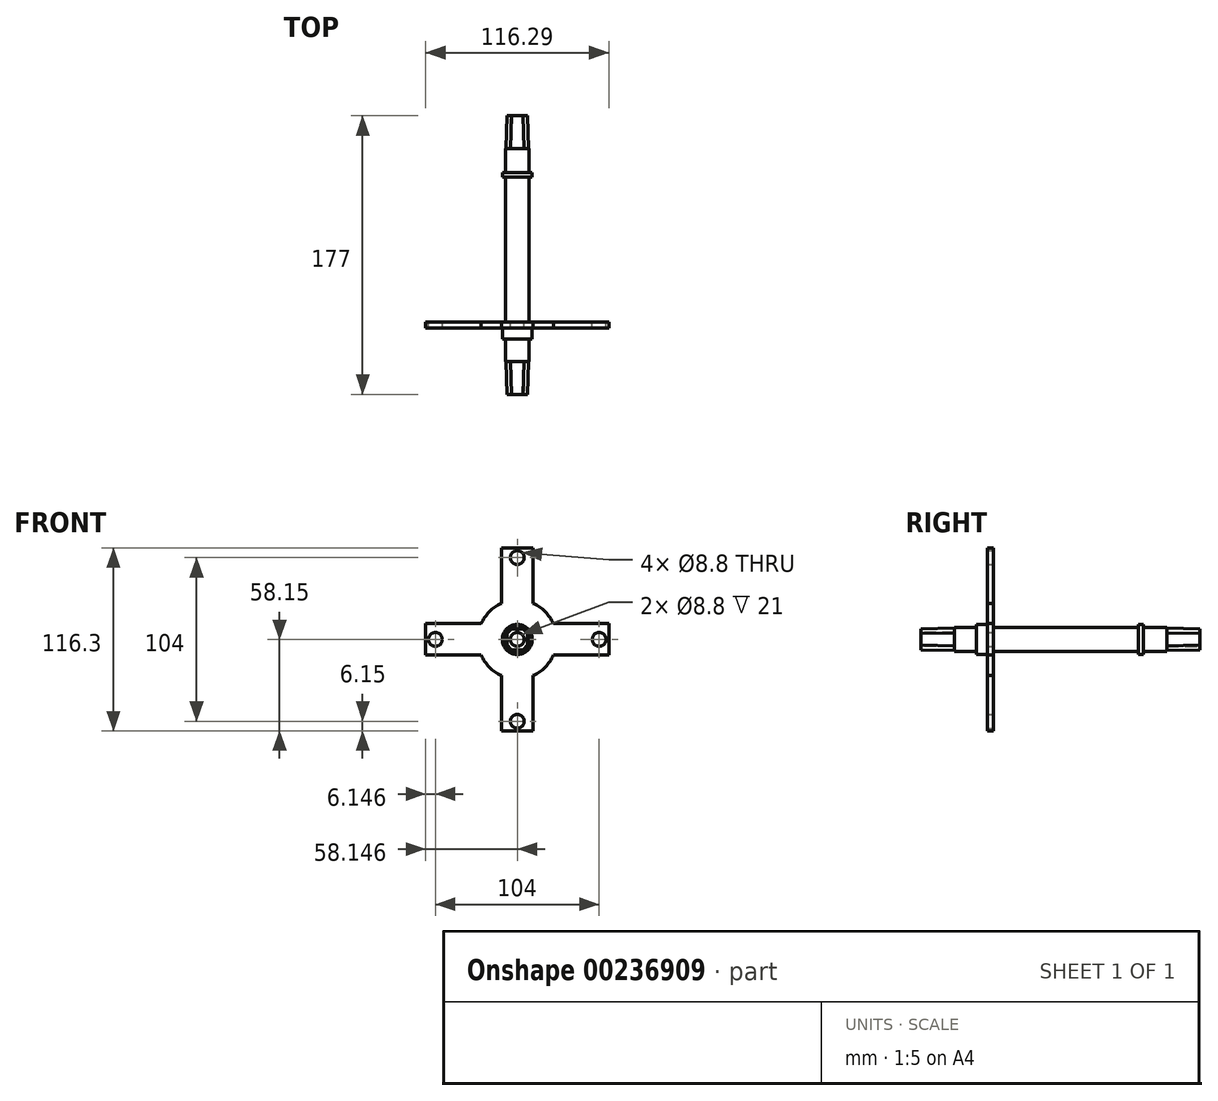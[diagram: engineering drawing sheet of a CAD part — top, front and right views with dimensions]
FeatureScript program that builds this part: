
annotation { "Feature Type Name" : "Feature", "Feature Type Description" : "" }
export const myFeature = defineFeature(function(context is Context, id is Id, definition is map)
    precondition{}
    {
        {
            var Q0;
            Q0=qCreatedBy(makeId("Front.planeOp"),FACE);
            cPlane(context, id + "F0", {"entities" : qUnion([Q0]), "cplaneType" : CPlaneType.OFFSET, "offset" : 135 * mm, "oppositeDirection" : true, "width" : 150 * mm, "height" : 150 * mm});
        }
        {
            var Q0;
            Q0=qCreatedBy(makeId("Front.planeOp"),FACE);
            cPlane(context, id + "F1", {"entities" : qUnion([Q0]), "cplaneType" : CPlaneType.OFFSET, "offset" : 67.5 * mm, "oppositeDirection" : true, "width" : 150 * mm, "height" : 150 * mm});
        }
        {
            var Q0;
            Q0=qCreatedBy(makeId("Front.planeOp"),FACE);
            cPlane(context, id + "F2", {"entities" : qUnion([Q0]), "cplaneType" : CPlaneType.OFFSET, "offset" : 21 * mm, "width" : 150 * mm, "height" : 150 * mm});
        }
        {
            var Q0;
            Q0=qCreatedBy(makeId("Front.planeOp"),FACE);
            var sketch = newSketch(context, id + "F3", { "sketchPlane" : qUnion([Q0])});
            skLineSegment(sketch, "E0.bottom", {"start": v(-101.97, -7.15) * mm, "end": v(-116.27, -7.15) * mm});
            skLineSegment(sketch, "E0.top", {"start": v(-101.97, 7.15) * mm, "end": v(-116.27, 7.15) * mm});
            skLineSegment(sketch, "E0.left", {"start": v(-101.97, -7.15) * mm, "end": v(-101.97, 7.15) * mm});
            skLineSegment(sketch, "E0.right", {"start": v(-116.27, -7.15) * mm, "end": v(-116.27, 7.15) * mm});
            skPoint(sketch, "E0.middle", {"position": v(-109.12, 0) * mm});
            skSolve(sketch);
        }
        {
            var Q0;
            Q0=qCreatedBy(id+"F2.planeOp",FACE);
            var sketch = newSketch(context, id + "F4", { "sketchPlane" : qUnion([Q0])});
            skLineSegment(sketch, "E1.bottom", {"start": v(-102.47, 6.65) * mm, "end": v(-115.77, 6.65) * mm});
            skLineSegment(sketch, "E1.top", {"start": v(-102.47, -6.65) * mm, "end": v(-115.77, -6.65) * mm});
            skLineSegment(sketch, "E1.left", {"start": v(-102.47, 6.65) * mm, "end": v(-102.47, -6.65) * mm});
            skLineSegment(sketch, "E1.right", {"start": v(-115.77, 6.65) * mm, "end": v(-115.77, -6.65) * mm});
            skPoint(sketch, "E1.middle", {"position": v(-109.12, 0) * mm});
            skSolve(sketch);
        }
        {
            var Q0;
            Q0=sQuery(id+"F4.wireOp",VERTEX,"E1.middle");
            var Q1;
            Q1=qCreatedBy(makeId("Right.planeOp"),FACE);
            cPlane(context, id + "F5", {"entities" : qUnion([Q0, Q1]), "cplaneType" : CPlaneType.PLANE_POINT, "offset" : 25 * mm, "width" : 150 * mm, "height" : 150 * mm});
        }
        {
            var Q0;
            Q0=qCreatedBy(id+"F5.planeOp",FACE);
            var sketch = newSketch(context, id + "F6", { "sketchPlane" : qUnion([Q0])});
            skLineSegment(sketch, "E2", {"start": v(-85.2, 0) * mm, "end": v(164.36, 0) * mm, "construction": true});
            skSolve(sketch);
        }
        {
            var Q0;
            Q0=makeQuery(id+"F3.imprint","IMPRINT",FACE,{"disambiguationData":[TD([[makeQuery(id+"F3.imprint","IMPRINT",EDGE,{"derivedFrom":sQuery(id+"F3.wireOp",EDGE,"E0.bottom")}),-1.0]])]});
            var Q1;
            Q1=makeQuery(id+"F4.imprint","IMPRINT",FACE,{"disambiguationData":[TD([[makeQuery(id+"F4.imprint","IMPRINT",EDGE,{"derivedFrom":sQuery(id+"F4.wireOp",EDGE,"E1.bottom")}),1.0]])]});
            loft(context, id + "F7", {"sheetProfilesArray" : [{ "sheetProfileEntities" : qUnion([Q0]) }, { "sheetProfileEntities" : qUnion([Q1]) }]});
        }
        {
            var Q0;
            Q0=makeQuery(id+"F7.opLoft","SWEPT_EDGE",EDGE,{"disambiguationData":[OSD([sQuery(id+"F3.wireOp",EDGE,"E0.top"),sQuery(id+"F3.wireOp",EDGE,"E0.right"),sQuery(id+"F4.wireOp",EDGE,"E1.bottom"),sQuery(id+"F4.wireOp",EDGE,"E1.right")])]});
            var Q1;
            Q1=makeQuery(id+"F7.opLoft","SWEPT_EDGE",EDGE,{"disambiguationData":[OSD([sQuery(id+"F3.wireOp",EDGE,"E0.bottom"),sQuery(id+"F3.wireOp",EDGE,"E0.right"),sQuery(id+"F4.wireOp",EDGE,"E1.top"),sQuery(id+"F4.wireOp",EDGE,"E1.right")])]});
            var Q2;
            Q2=makeQuery(id+"F7.opLoft","SWEPT_EDGE",EDGE,{"disambiguationData":[OSD([sQuery(id+"F3.wireOp",EDGE,"E0.top"),sQuery(id+"F3.wireOp",EDGE,"E0.left"),sQuery(id+"F4.wireOp",EDGE,"E1.bottom"),sQuery(id+"F4.wireOp",EDGE,"E1.left")])]});
            var Q3;
            Q3=makeQuery(id+"F7.opLoft","SWEPT_EDGE",EDGE,{"disambiguationData":[OSD([sQuery(id+"F3.wireOp",EDGE,"E0.bottom"),sQuery(id+"F3.wireOp",EDGE,"E0.left"),sQuery(id+"F4.wireOp",EDGE,"E1.top"),sQuery(id+"F4.wireOp",EDGE,"E1.left")])]});
            chamfer(context, id + "F8", {"entities" : qUnion([Q0, Q1, Q2, Q3]), "width" : 3 * mm, "tangentPropagation" : true});
        }
        {
            var Q0;
            Q0=qCreatedBy(makeId("Front.planeOp"),FACE);
            var sketch = newSketch(context, id + "F9", { "sketchPlane" : qUnion([Q0])});
            skCircle(sketch, "E3", {"center": v(-109.12, 0) * mm, "radius": 7.5 * mm});
            skCircle(sketch, "E4", {"center": v(-109.12, 0) * mm, "radius": 9.5 * mm});
            skSolve(sketch);
        }
        {
            var Q0;
            Q0=makeQuery(id+"F9.imprint","IMPRINT",FACE,{"disambiguationData":[TD([[makeQuery(id+"F9.imprint","IMPRINT",EDGE,{"derivedFrom":sQuery(id+"F9.wireOp",EDGE,"E3")}),1.0]])]});
            var Q1;
            Q1=qCreatedBy(id+"F0.planeOp",FACE);
            extrude(context, id + "F10", {"entities" : qUnion([Q0]), "endBound" : BoundingType.UP_TO_SURFACE, "oppositeDirection" : true, "endBoundEntityFace" : qUnion([Q1]), "depth" : 25 * mm});
        }
        {
            var Q0;
            Q0=makeQuery(id+"F9.imprint","IMPRINT",FACE,{"disambiguationData":[TD([[makeQuery(id+"F9.imprint","IMPRINT",EDGE,{"derivedFrom":sQuery(id+"F9.wireOp",EDGE,"E3")}),-1.0]])]});
            extrude(context, id + "F11", {"entities" : qUnion([Q0]), "operationType" : NewBodyOperationType.ADD, "oppositeDirection" : true, "depth" : 25 * mm, "hasSecondDirection" : true, "secondDirectionOppositeDirection" : true, "secondDirectionDepth" : 14 * mm});
        }
        {
            var Q0;
            Q0=makeQuery(id+"F9.imprint","IMPRINT",FACE,{"disambiguationData":[TD([[makeQuery(id+"F9.imprint","IMPRINT",EDGE,{"derivedFrom":sQuery(id+"F9.wireOp",EDGE,"E3")}),-1.0]])]});
            extrude(context, id + "F12", {"entities" : qUnion([Q0]), "operationType" : NewBodyOperationType.ADD, "oppositeDirection" : true, "depth" : 120 * mm, "hasSecondDirection" : true, "secondDirectionOppositeDirection" : true, "secondDirectionDepth" : 117 * mm});
        }
        {
            var Q0;
            Q0=makeQuery(id+"F11.opExtrude","CAP_FACE",FACE,{"disambiguationData":[OSD([sQuery(id+"F9.wireOp",EDGE,"E3"),sQuery(id+"F9.wireOp",EDGE,"E4")])],"isStart":false});
            var sketch = newSketch(context, id + "F13", { "sketchPlane" : qUnion([Q0])});
            skCircle(sketch, "E5", {"center": v(109.12, 0) * mm, "radius": 59 * mm});
            skCircle(sketch, "E6", {"center": v(109.12, 0) * mm, "radius": 25 * mm});
            skLineSegment(sketch, "E7", {"start": v(109.12, 0) * mm, "end": v(109.12, 52) * mm, "construction": true});
            skLineSegment(sketch, "E8", {"start": v(109.12, 52) * mm, "end": v(109.12, 71.08) * mm, "construction": true});
            skLineSegment(sketch, "E9", {"start": v(119.12, 58.15) * mm, "end": v(119.12, 22.91) * mm});
            skLineSegment(sketch, "E10", {"start": v(119.12, 22.91) * mm, "end": v(99.12, 22.91) * mm});
            skLineSegment(sketch, "E11", {"start": v(99.12, 22.91) * mm, "end": v(99.12, 58.15) * mm});
            skLineSegment(sketch, "E12", {"start": v(99.12, 58.15) * mm, "end": v(119.12, 58.15) * mm});
            skLineSegment(sketch, "E13.1.0", {"start": v(132.04, 10) * mm, "end": v(167.27, 10) * mm});
            skLineSegment(sketch, "E13.1.1", {"start": v(109.12, 0) * mm, "end": v(161.12, 0) * mm, "construction": true});
            skLineSegment(sketch, "E13.1.2", {"start": v(167.27, -10) * mm, "end": v(132.04, -10) * mm});
            skLineSegment(sketch, "E13.1.3", {"start": v(167.27, 10) * mm, "end": v(167.27, -10) * mm});
            skLineSegment(sketch, "E13.2.0", {"start": v(119.12, -22.91) * mm, "end": v(119.12, -58.15) * mm});
            skLineSegment(sketch, "E13.2.1", {"start": v(109.12, 0) * mm, "end": v(109.12, -52) * mm, "construction": true});
            skLineSegment(sketch, "E13.2.2", {"start": v(99.12, -58.15) * mm, "end": v(99.12, -22.91) * mm});
            skLineSegment(sketch, "E13.2.3", {"start": v(119.12, -58.15) * mm, "end": v(99.12, -58.15) * mm});
            skLineSegment(sketch, "E13.3.0", {"start": v(86.21, -10) * mm, "end": v(50.98, -10) * mm});
            skLineSegment(sketch, "E13.3.1", {"start": v(109.12, 0) * mm, "end": v(57.12, 0) * mm, "construction": true});
            skLineSegment(sketch, "E13.3.2", {"start": v(50.98, 10) * mm, "end": v(86.21, 10) * mm});
            skLineSegment(sketch, "E13.3.3", {"start": v(50.98, -10) * mm, "end": v(50.98, 10) * mm});
            skLineSegment(sketch, "E13.anchor1", {"start": v(109.12, 0) * mm, "end": v(99.12, 22.91) * mm, "construction": true});
            skLineSegment(sketch, "E13.anchor2", {"start": v(109.12, 0) * mm, "end": v(86.21, -10) * mm, "construction": true});
            skSolve(sketch);
        }
        {
            var Q0;
            {var subQ1=sQuery(id+"F13.wireOp",EDGE,"E9");Q0=makeQuery(id+"F13.imprint","IMPRINT",FACE,{"disambiguationData":[TD([[makeQuery(id+"F13.imprint","IMPRINT",EDGE,{"derivedFrom":subQ1}),-1.0]])]});}
            var Q1;
            {var subQ0=sQuery(id+"F13.wireOp",EDGE,"E13.2.0");Q1=makeQuery(id+"F13.imprint","IMPRINT",FACE,{"disambiguationData":[TD([[makeQuery(id+"F13.imprint","IMPRINT",EDGE,{"derivedFrom":subQ0}),-1.0]])]});}
            var Q2;
            {var subQ0=sQuery(id+"F13.wireOp",EDGE,"E13.1.0");Q2=makeQuery(id+"F13.imprint","IMPRINT",FACE,{"disambiguationData":[TD([[makeQuery(id+"F13.imprint","IMPRINT",EDGE,{"derivedFrom":subQ0}),-1.0]])]});}
            var Q3;
            {var subQ4=sQuery(id+"F13.wireOp",EDGE,"E10");Q3=makeQuery(id+"F13.imprint","IMPRINT",FACE,{"disambiguationData":[TD([[makeQuery(id+"F13.imprint","IMPRINT",EDGE,{"derivedFrom":subQ4}),1.0]])]});}
            var Q4;
            {var subQ0=sQuery(id+"F13.wireOp",EDGE,"E13.3.0");Q4=makeQuery(id+"F13.imprint","IMPRINT",FACE,{"disambiguationData":[TD([[makeQuery(id+"F13.imprint","IMPRINT",EDGE,{"derivedFrom":subQ0}),-1.0]])]});}
            var Q5;
            {var subQ0=sQuery(id+"F13.wireOp",EDGE,"E10");Q5=makeQuery(id+"F13.imprint","IMPRINT",FACE,{"disambiguationData":[TD([[makeQuery(id+"F13.imprint","IMPRINT",EDGE,{"derivedFrom":subQ0}),-1.0]])]});}
            extrude(context, id + "F14", {"entities" : qUnion([Q0, Q1, Q2, Q3, Q4, Q5]), "operationType" : NewBodyOperationType.ADD, "oppositeDirection" : true, "depth" : 4 * mm});
        }
        {
            var Q0;
            Q0=sQuery(id+"F13.wireOp",VERTEX,"E8.start");
            var Q1;
            Q1=sQuery(id+"F13.wireOp",VERTEX,"E13.3.1.end");
            var Q2;
            Q2=sQuery(id+"F13.wireOp",VERTEX,"E13.1.1.end");
            var Q3;
            Q3=sQuery(id+"F13.wireOp",VERTEX,"E13.2.1.end");
            var Q4;
            Q4=makeQuery(id+"F10.opExtrude","SWEPT_BODY",BODY,{"disambiguationData":[OSD([sQuery(id+"F9.wireOp",EDGE,"E3")])]});
            hole(context, id + "F15", {"style" : HoleStyle.SIMPLE, "endStyle" : HoleEndStyle.THROUGH, "standardTappedOrClearance" : lookupTablePath({ "standard" : "ISO", "fit" : "Normal", "size" : "M8", "type" : "Clearance" }), "standardBlindInLast" : lookupTablePath({ "fit" : "Standard", "standard" : "ISO", "size" : "M8", "type" : "Clearance" }), "holeDiameter" : 8.8 * mm, "locations" : qUnion([Q0, Q1, Q2, Q3]), "scope" : qUnion([Q4]), "isTappedThrough" : true});
        }
        {
            var Q0;
            Q0=sQuery(id+"F4.wireOp",VERTEX,"E1.middle");
            var Q1;
            Q1=makeQuery(id+"F7.opLoft","SWEPT_BODY",BODY,{"disambiguationData":[OSD([makeQuery(id+"F3.imprint","IMPRINT",FACE,{"disambiguationData":[TD([[makeQuery(id+"F3.imprint","IMPRINT",EDGE,{"derivedFrom":sQuery(id+"F3.wireOp",EDGE,"E0.bottom")}),-1.0]])]}),makeQuery(id+"F4.imprint","IMPRINT",FACE,{"disambiguationData":[TD([[makeQuery(id+"F4.imprint","IMPRINT",EDGE,{"derivedFrom":sQuery(id+"F4.wireOp",EDGE,"E1.bottom")}),1.0]])]})])]});
            hole(context, id + "F16", {"style" : HoleStyle.SIMPLE, "endStyle" : HoleEndStyle.THROUGH, "standardTappedOrClearance" : lookupTablePath({ "standard" : "ISO", "fit" : "Normal", "size" : "M8", "type" : "Clearance" }), "standardBlindInLast" : lookupTablePath({ "fit" : "Standard", "standard" : "ISO", "size" : "M8", "type" : "Clearance" }), "holeDiameter" : 8.8 * mm, "locations" : qUnion([Q0]), "scope" : qUnion([Q1]), "isTappedThrough" : true});
        }
        {
            var Q0;
            Q0=makeQuery(id+"F7.opLoft","SWEPT_BODY",BODY,{"disambiguationData":[OSD([makeQuery(id+"F3.imprint","IMPRINT",FACE,{"disambiguationData":[TD([[makeQuery(id+"F3.imprint","IMPRINT",EDGE,{"derivedFrom":sQuery(id+"F3.wireOp",EDGE,"E0.bottom")}),-1.0]])]}),makeQuery(id+"F4.imprint","IMPRINT",FACE,{"disambiguationData":[TD([[makeQuery(id+"F4.imprint","IMPRINT",EDGE,{"derivedFrom":sQuery(id+"F4.wireOp",EDGE,"E1.bottom")}),1.0]])]})])]});
            var Q1;
            Q1=qCreatedBy(id+"F1.planeOp",FACE);
            mirror(context, id + "F17", {"operationType" : NewBodyOperationType.ADD, "entities" : qUnion([Q0]), "mirrorPlane" : qUnion([Q1])});
        }
    });
